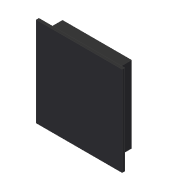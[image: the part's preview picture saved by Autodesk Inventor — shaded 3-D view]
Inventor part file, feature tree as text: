
AUTODESK INVENTOR PART (.ipt)
format: ipt  version: 2017 (Build 210142000, 142)  size: 137,216 bytes
history: native  units: mm
features: projected_geometry x4, sketch x3, extrude x3
ambient origin geometry x8: Origin, YZ Plane, XZ Plane, XY Plane, X Axis, Y Axis, Z Axis, Center Point
bodies: Solid1 (feature_tree)
feature tree (10):
  sketch  "Sketch1"  dims[d0=15.5mm d1=17.25mm]
  extrude  "Extrusion1"  Depth=17.25mm
  extrude  "Extrusion2"  Depth=14.5mm
  sketch  "Sketch2"  dims[d2=14.5mm d3=42.5mm]
  extrude  "Extrusion3"  Depth=10.0mm
  projected_geometry  "Projected Loop1"
  projected_geometry  "Projected Loop2"
  sketch  "Sketch3"  dims[d4=1.0mm d5=10.0mm d6=10.0mm d7=1.0mm d8=1.0mm d9=1.0mm d10=28.25mm d11=1.0mm d12=0.0mm d13=7.0mm d14=0.0mm d15=8.625mm d16=22.5mm d17=8.625mm d18=10.0mm d19=0.0mm]
  projected_geometry  "Projected Loop3"
  projected_geometry  "Projected Loop4"
